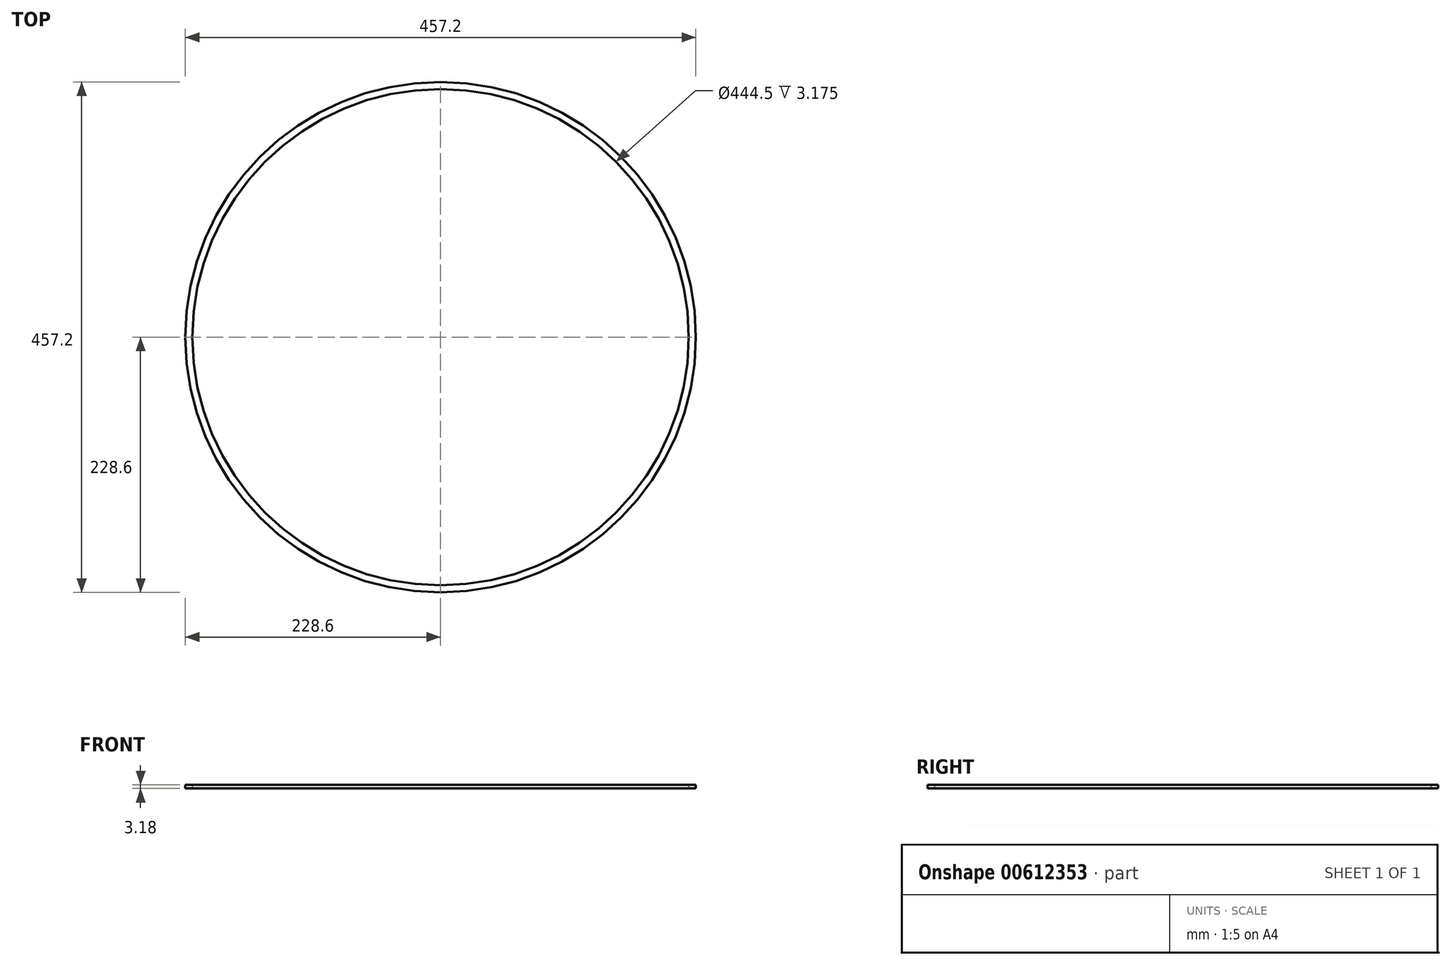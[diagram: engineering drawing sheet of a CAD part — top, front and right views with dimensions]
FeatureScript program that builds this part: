
annotation { "Feature Type Name" : "Feature", "Feature Type Description" : "" }
export const myFeature = defineFeature(function(context is Context, id is Id, definition is map)
    precondition{}
    {
        {
            var Q0;
            Q0=qCreatedBy(makeId("Front.planeOp"),FACE);
            var sketch = newSketch(context, id + "F0", { "sketchPlane" : qUnion([Q0])});
            skLineSegment(sketch, "E0", {"start": v(0, 0) * mm, "end": v(0, 277.21) * mm});
            skLineSegment(sketch, "E1.bottom", {"start": v(222.25, 0) * mm, "end": v(228.6, 0) * mm});
            skLineSegment(sketch, "E1.top", {"start": v(222.25, 3.18) * mm, "end": v(228.6, 3.18) * mm});
            skLineSegment(sketch, "E1.left", {"start": v(222.25, 0) * mm, "end": v(222.25, 3.18) * mm});
            skLineSegment(sketch, "E1.right", {"start": v(228.6, 0) * mm, "end": v(228.6, 3.18) * mm});
            skSolve(sketch);
        }
        {
            var Q0;
            Q0=makeQuery(id+"F0.imprint","IMPRINT",FACE,{"disambiguationData":[TD([[makeQuery(id+"F0.imprint","IMPRINT",EDGE,{"derivedFrom":sQuery(id+"F0.wireOp",EDGE,"E1.bottom")}),1.0]])]});
            var Q1;
            Q1=sQuery(id+"F0.wireOp",EDGE,"E0");
            revolve(context, id + "F1", {"entities" : qUnion([Q0]), "axis" : qUnion([Q1]), "revolveType" : RevolveType.FULL});
        }
    });
